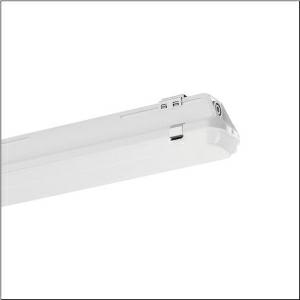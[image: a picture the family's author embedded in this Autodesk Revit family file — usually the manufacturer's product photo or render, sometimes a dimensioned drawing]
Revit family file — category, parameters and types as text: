
# Revit family: monsun_21_emergency_51fb10dp487c3h
name_source: partatom
category: Lighting Fixtures
units: mm (PartAtom-declared; Revit-internal decimal feet)

## family parameters
Cut with Voids When Loaded = No
Host = Face
Light Source = No
Part Type = Normal
Room Calculation Point = No
Round Connector Dimension = Use Diameter
Shared = No

## types (1)
- --- (1 x LED, 8090 lm, 49.9 W, 4000K)
    Apparent Load = 50 VA
    CIE Flux Codes = 47 77 93 94 100
    Color Rendering = 80
    Color Temperature = 4000K
    Default Elevation = 1800 mm
    Description = Monsun 21 emergency, damp-proof luminaire, chain hanger, primary optical cover: enclosure, of PMMA, light emission: direct distribution, primary light characteristic: symmetric, installation type: vertical mounting, horizontal mounting, surface-mounted, suspended mounting, LED, rated luminous flux: 8.090lm, luminous efficacy: 176lm/W, light colour: 840, colour temperature: 4000K, control gear: DALI 2, with terminal, 5+3-pole, max. 2.5mm², mains connection: 220..240V, AC, 50/60Hz, rated input power: 50W, control gear: single battery element, battery: LiFePO4, 9Ah, housing, of glass-fibre reinforced polyester, uncoated, bright grey, incl. chain hanger, length: 1.590mm, width: 90mm, height: 88mm, clip for enclosure, of stainless steel (V2A), ceiling mounting element, of stainless steel (V2A), chain hanger, of stainless steel (V2A), protection rating (complete): IP66, insulation class (complete): insulation class I (protective earthing), certification: CE, UKCA, protection symbol: D, impact resistance: IK04, permissible operating ambient temperature: +5..+25°C, standard: EN 50419, EN 60598-2-1, EN 60598-2-22, corresponds to IFS (International Featured Standards) requirements for safety and quality in the food industry, for indoor or canopied outdoor use, no direct snow, no direct sun, no direct rain, LABS conformity tested according to VDMA 24364:2018-05, contact your sales advisor before using the luminaires in applications with unclear chemical exposure, large temperature fluctuations or condensation-forming humidity, packaging unit: 1 piece
    Height = 89 mm
    Lamp = 1 x LED
    Lamp Light Flux = 8090 lm
    Lamp Power = 49.9 W
    Lamp count = 1
    Length = 1590 mm
    Luminous efficacy = 162 lm/W
    Manufacturer = Siteco
    ModVariant = No
    Model = 51FB10DP487C3H
    Mounting Place = Ceiling
    Mounting Type = Surface mounted
    Number of Poles = 1
    OnlyDefault = Yes
    Power Factor = 1
    Product Name = Monsun 21 emergency
    Product group = damp-proof luminaire
    ProductGroupID = 300
    Protection Class = Protection class I
    Protection Degree = IP 66
    RLX_Detail_Level = 1
    RLX_Emergency_Light_Flux = 0 lm
    RLX_Emergency_Type = 0
    RLX_Emergency_Type_DB = No
    RlxData = <blob elided: 92733 chars, md5=d11a2a17>
    Socket = socket
    Standby Power = 0 W
    System Light Flux = 8090 lm
    System Power = 50 W
    Type Comments = : luminous flux: 100 % | dim-lin: 254 | 311 mA
    Type Image = l_1319656.jpg
    URL = http://relux.com
    VarID = @adj_038193
    Voltage = 0 V
    Weight = 0.00 kg
    Width = 90 mm

## geometry (parser evidence)
native form markers: Blend x4, Sweep x13
no freeform markers — native parametric forms only
